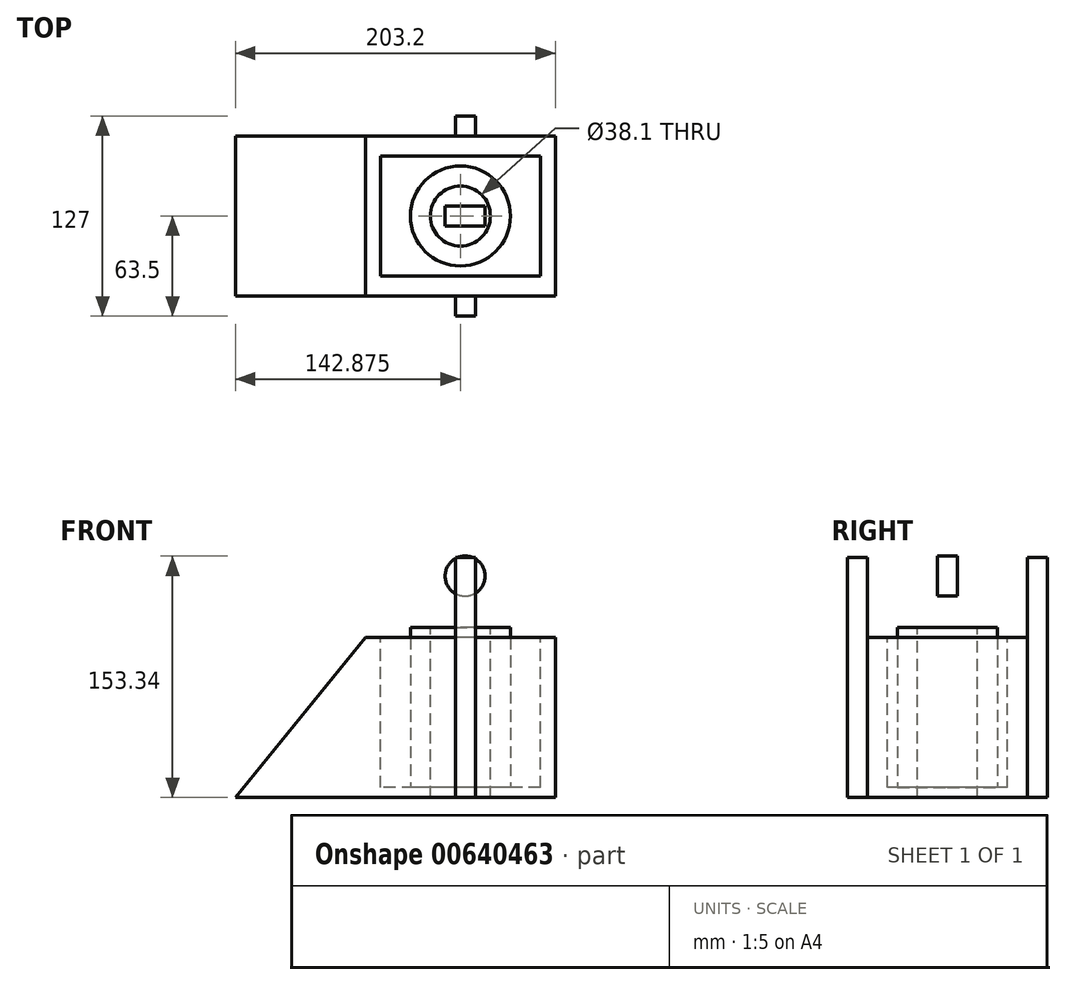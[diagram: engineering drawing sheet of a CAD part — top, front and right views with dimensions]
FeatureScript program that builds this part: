
annotation { "Feature Type Name" : "Feature", "Feature Type Description" : "" }
export const myFeature = defineFeature(function(context is Context, id is Id, definition is map)
    precondition{}
    {
        {
            var Q0;
            Q0=qCreatedBy(makeId("Front.planeOp"),FACE);
            var sketch = newSketch(context, id + "F0", { "sketchPlane" : qUnion([Q0])});
            skLineSegment(sketch, "E0", {"start": v(0, 0) * mm, "end": v(203.2, 0) * mm});
            skLineSegment(sketch, "E1", {"start": v(203.2, 0) * mm, "end": v(203.2, 101.6) * mm});
            skPoint(sketch, "E2.endSnap0", {"position": v(101.6, 0) * mm});
            skLineSegment(sketch, "E3", {"start": v(203.2, 101.6) * mm, "end": v(82.55, 101.6) * mm});
            skLineSegment(sketch, "E4", {"start": v(82.55, 101.6) * mm, "end": v(0, 0) * mm});
            skSolve(sketch);
        }
        {
            var Q0;
            Q0=makeQuery(id+"F0.imprint","IMPRINT",FACE,{"disambiguationData":[TD([[makeQuery(id+"F0.imprint","IMPRINT",EDGE,{"derivedFrom":sQuery(id+"F0.wireOp",EDGE,"E0")}),1.0]])]});
            extrude(context, id + "F1", {"entities" : qUnion([Q0]), "oppositeDirection" : true, "depth" : 101.6 * mm, "offsetDistance" : 25.4 * mm});
        }
        {
            var Q0;
            Q0=makeQuery(id+"F1.opExtrude","SWEPT_FACE",FACE,{"disambiguationData":[OSD([sQuery(id+"F0.wireOp",EDGE,"E3")])]});
            var sketch = newSketch(context, id + "F2", { "sketchPlane" : qUnion([Q0])});
            skLineSegment(sketch, "E5.bottom", {"start": v(193.68, 88.96) * mm, "end": v(92.08, 88.96) * mm});
            skLineSegment(sketch, "E5.top", {"start": v(193.68, 12.64) * mm, "end": v(92.08, 12.64) * mm});
            skLineSegment(sketch, "E5.left", {"start": v(193.68, 88.96) * mm, "end": v(193.68, 12.64) * mm});
            skLineSegment(sketch, "E5.right", {"start": v(92.08, 88.96) * mm, "end": v(92.08, 12.64) * mm});
            skPoint(sketch, "E5.middle", {"position": v(142.88, 50.8) * mm});
            skPoint(sketch, "E5.middle.positionSnap0", {"position": v(203.2, 50.8) * mm});
            skPoint(sketch, "E5.middle.positionSnap1", {"position": v(142.88, 101.6) * mm});
            skPoint(sketch, "E5.centerSnap0", {"position": v(203.2, 50.8) * mm});
            skPoint(sketch, "E5.centerSnap1", {"position": v(142.88, 101.6) * mm});
            skSolve(sketch);
        }
        {
            var Q0;
            Q0=makeQuery(id+"F2.imprint","IMPRINT",FACE,{"disambiguationData":[TD([[makeQuery(id+"F2.imprint","IMPRINT",EDGE,{"derivedFrom":sQuery(id+"F2.wireOp",EDGE,"E5.bottom")}),1.0]])]});
            extrude(context, id + "F3", {"entities" : qUnion([Q0]), "operationType" : NewBodyOperationType.REMOVE, "oppositeDirection" : true, "depth" : 95.25 * mm, "offsetDistance" : 25.4 * mm});
        }
        {
            var Q0;
            Q0=makeQuery(id+"F3.boolean.opBoolean","COPY",FACE,{"derivedFrom":makeQuery(id+"F3.opExtrude","CAP_FACE",FACE,{"disambiguationData":[OSD([sQuery(id+"F2.wireOp",EDGE,"E5.bottom"),sQuery(id+"F2.wireOp",EDGE,"E5.top"),sQuery(id+"F2.wireOp",EDGE,"E5.left"),sQuery(id+"F2.wireOp",EDGE,"E5.right")])],"isStart":false})});
            var sketch = newSketch(context, id + "F4", { "sketchPlane" : qUnion([Q0])});
            skCircle(sketch, "E6", {"center": v(142.88, 50.8) * mm, "radius": 31.75 * mm});
            skPoint(sketch, "E6.centerSnap0", {"position": v(193.68, 50.8) * mm});
            skPoint(sketch, "E6.centerSnap1", {"position": v(142.88, 88.96) * mm});
            skSolve(sketch);
        }
        {
            var Q0;
            Q0=makeQuery(id+"F4.imprint","IMPRINT",FACE,{"disambiguationData":[TD([[makeQuery(id+"F4.imprint","IMPRINT",EDGE,{"derivedFrom":sQuery(id+"F4.wireOp",EDGE,"E6")}),1.0]])]});
            extrude(context, id + "F5", {"entities" : qUnion([Q0]), "operationType" : NewBodyOperationType.ADD, "depth" : 101.6 * mm, "offsetDistance" : 25.4 * mm});
        }
        {
            var Q0;
            Q0=makeQuery(id+"F5.opExtrude","CAP_FACE",FACE,{"disambiguationData":[OSD([sQuery(id+"F4.wireOp",EDGE,"E6")])],"isStart":false});
            var sketch = newSketch(context, id + "F6", { "sketchPlane" : qUnion([Q0])});
            skCircle(sketch, "E7", {"center": v(142.88, 50.8) * mm, "radius": 19.05 * mm});
            skSolve(sketch);
        }
        {
            var Q0;
            Q0 = qSketchRegion(id + "F6", true);
            extrude(context, id + "F7", {"entities" : qUnion([Q0]), "operationType" : NewBodyOperationType.REMOVE, "oppositeDirection" : true, "depth" : 159 * mm, "offsetDistance" : 25.4 * mm});
        }
        {
            var Q0;
            Q0=makeQuery(id+"F1.opExtrude","CAP_FACE",FACE,{"disambiguationData":[OSD([sQuery(id+"F0.wireOp",EDGE,"E0"),sQuery(id+"F0.wireOp",EDGE,"E1"),sQuery(id+"F0.wireOp",EDGE,"E3"),sQuery(id+"F0.wireOp",EDGE,"E4")])],"isStart":false});
            var sketch = newSketch(context, id + "F8", { "sketchPlane" : qUnion([Q0])});
            skSolve(sketch);
        }
        {
            var Q0;
            Q0=makeQuery(id+"F8.imprint","IMPRINT",FACE,{"disambiguationData":[TD([[makeQuery(id+"F8.imprint","IMPRINT",EDGE,{"derivedFrom":makeQuery(id+"F1.opExtrude","CAP_EDGE",EDGE,{"disambiguationData":[OSD([sQuery(id+"F0.wireOp",EDGE,"E0")])],"isStart":false})}),-1.0]])]});
            var sketch = newSketch(context, id + "F9", { "sketchPlane" : qUnion([Q0])});
            skPoint(sketch, "E8.0", {"position": v(-203.2, 0) * mm});
            skPoint(sketch, "E9.0", {"position": v(-203.2, 101.6) * mm});
            skLineSegment(sketch, "E10.0", {"start": v(-203.2, 101.6) * mm, "end": v(-82.55, 101.6) * mm});
            skLineSegment(sketch, "E11", {"start": v(-203.2, 0) * mm, "end": v(-152.4, 0) * mm});
            skLineSegment(sketch, "E12", {"start": v(-152.4, 0) * mm, "end": v(-152.4, 101.6) * mm});
            skLineSegment(sketch, "E13", {"start": v(-152.4, 0) * mm, "end": v(-139.7, 0) * mm});
            skLineSegment(sketch, "E14", {"start": v(-139.7, 0) * mm, "end": v(-139.7, 101.6) * mm});
            skLineSegment(sketch, "E15", {"start": v(-152.4, 101.6) * mm, "end": v(-152.4, 152.4) * mm});
            skLineSegment(sketch, "E16", {"start": v(-152.4, 152.4) * mm, "end": v(-139.7, 152.4) * mm});
            skLineSegment(sketch, "E17", {"start": v(-139.7, 152.4) * mm, "end": v(-139.7, 101.6) * mm});
            skSolve(sketch);
        }
        {
            var Q0;
            Q0 = qSketchRegion(id + "F9", true);
            extrude(context, id + "F10", {"entities" : qUnion([Q0]), "operationType" : NewBodyOperationType.ADD, "depth" : 12.7 * mm, "offsetDistance" : 25.4 * mm});
        }
        {
            var Q0;
            Q0=makeQuery(id+"F1.opExtrude","CAP_FACE",FACE,{"disambiguationData":[OSD([sQuery(id+"F0.wireOp",EDGE,"E0"),sQuery(id+"F0.wireOp",EDGE,"E1"),sQuery(id+"F0.wireOp",EDGE,"E3"),sQuery(id+"F0.wireOp",EDGE,"E4")])],"isStart":true});
            var sketch = newSketch(context, id + "F11", { "sketchPlane" : qUnion([Q0])});
            skLineSegment(sketch, "E18", {"start": v(203.2, 0) * mm, "end": v(152.4, 0) * mm});
            skLineSegment(sketch, "E19", {"start": v(152.4, 0) * mm, "end": v(152.4, 101.6) * mm});
            skLineSegment(sketch, "E20", {"start": v(139.7, 101.6) * mm, "end": v(139.7, 0) * mm});
            skLineSegment(sketch, "E21", {"start": v(139.7, 0) * mm, "end": v(152.4, 0) * mm});
            skLineSegment(sketch, "E22", {"start": v(139.7, 101.6) * mm, "end": v(139.7, 152.4) * mm});
            skLineSegment(sketch, "E23", {"start": v(139.7, 152.4) * mm, "end": v(152.4, 152.4) * mm});
            skLineSegment(sketch, "E24", {"start": v(152.4, 152.4) * mm, "end": v(152.4, 101.6) * mm});
            skSolve(sketch);
        }
        {
            var Q0;
            Q0 = qSketchRegion(id + "F11", true);
            extrude(context, id + "F12", {"entities" : qUnion([Q0]), "operationType" : NewBodyOperationType.ADD, "depth" : 12.7 * mm, "offsetDistance" : 25.4 * mm});
        }
        {
            var Q0;
            Q0=makeQuery(id+"F12.opExtrude","CAP_FACE",FACE,{"disambiguationData":[OSD([sQuery(id+"F11.wireOp",EDGE,"E19"),sQuery(id+"F11.wireOp",EDGE,"E20"),sQuery(id+"F11.wireOp",EDGE,"E21"),sQuery(id+"F11.wireOp",EDGE,"E22"),sQuery(id+"F11.wireOp",EDGE,"E23"),sQuery(id+"F11.wireOp",EDGE,"E24")])],"isStart":false});
            var sketch = newSketch(context, id + "F13", { "sketchPlane" : qUnion([Q0])});
            skLineSegment(sketch, "E25", {"start": v(139.7, 152.4) * mm, "end": v(146.05, 152.4) * mm});
            skLineSegment(sketch, "E26", {"start": v(146.05, 152.4) * mm, "end": v(146.05, 139.7) * mm});
            skCircle(sketch, "E27", {"center": v(146.05, 139.7) * mm, "radius": 1.27 * mm});
            skSolve(sketch);
        }
        {
            var Q0;
            Q0=sQuery(id+"F13.wireOp",EDGE,"E27");
            extrude(context, id + "F14", {"bodyType" : ToolBodyType.SURFACE, "surfaceEntities" : qUnion([Q0]), "oppositeDirection" : true, "depth" : 127 * mm, "offsetDistance" : 25.4 * mm});
        }
        {
            var Q0;
            Q0=makeQuery(id+"F14.opExtrude","SWEPT_FACE",FACE,{"disambiguationData":[OSD([sQuery(id+"F13.wireOp",EDGE,"E27")])]});
            cPlane(context, id + "F15", {"entities" : qUnion([Q0]), "cplaneType" : CPlaneType.LINE_ANGLE, "offset" : 25.4 * mm, "angle" : 0 * degree, "width" : 152.4 * mm, "height" : 152.4 * mm});
        }
        {
            var Q0;
            Q0=qCreatedBy(makeId("Front.planeOp"),FACE);
            cPlane(context, id + "F16", {"entities" : qUnion([Q0]), "cplaneType" : CPlaneType.OFFSET, "offset" : 50.8 * mm, "oppositeDirection" : true, "width" : 152.4 * mm, "height" : 152.4 * mm});
        }
        {
            var Q0;
            Q0=qCreatedBy(id+"F16.planeOp",FACE);
            var sketch = newSketch(context, id + "F17", { "sketchPlane" : qUnion([Q0])});
            skCircle(sketch, "E28", {"center": v(145.87, 140.64) * mm, "radius": 12.7 * mm});
            skSolve(sketch);
        }
        {
            var Q0;
            Q0 = qSketchRegion(id + "F17", true);
            extrude(context, id + "F18", {"entities" : qUnion([Q0]), "oppositeDirection" : true, "depth" : 6.35 * mm, "offsetDistance" : 25.4 * mm});
        }
        {
            var Q0;
            Q0=makeQuery(id+"F18.opExtrude","CAP_FACE",FACE,{"disambiguationData":[OSD([sQuery(id+"F17.wireOp",EDGE,"E28")])],"isStart":true});
            extrude(context, id + "F19", {"entities" : qUnion([Q0]), "operationType" : NewBodyOperationType.ADD, "depth" : 6.35 * mm, "offsetDistance" : 25.4 * mm});
        }
        {
            var Q0;
            Q0=qCreatedBy(makeId("Right.planeOp"),FACE);
            cPlane(context, id + "F20", {"entities" : qUnion([Q0]), "cplaneType" : CPlaneType.OFFSET, "offset" : 57.15 * mm, "oppositeDirection" : true, "width" : 152.4 * mm, "height" : 152.4 * mm});
        }
    });
